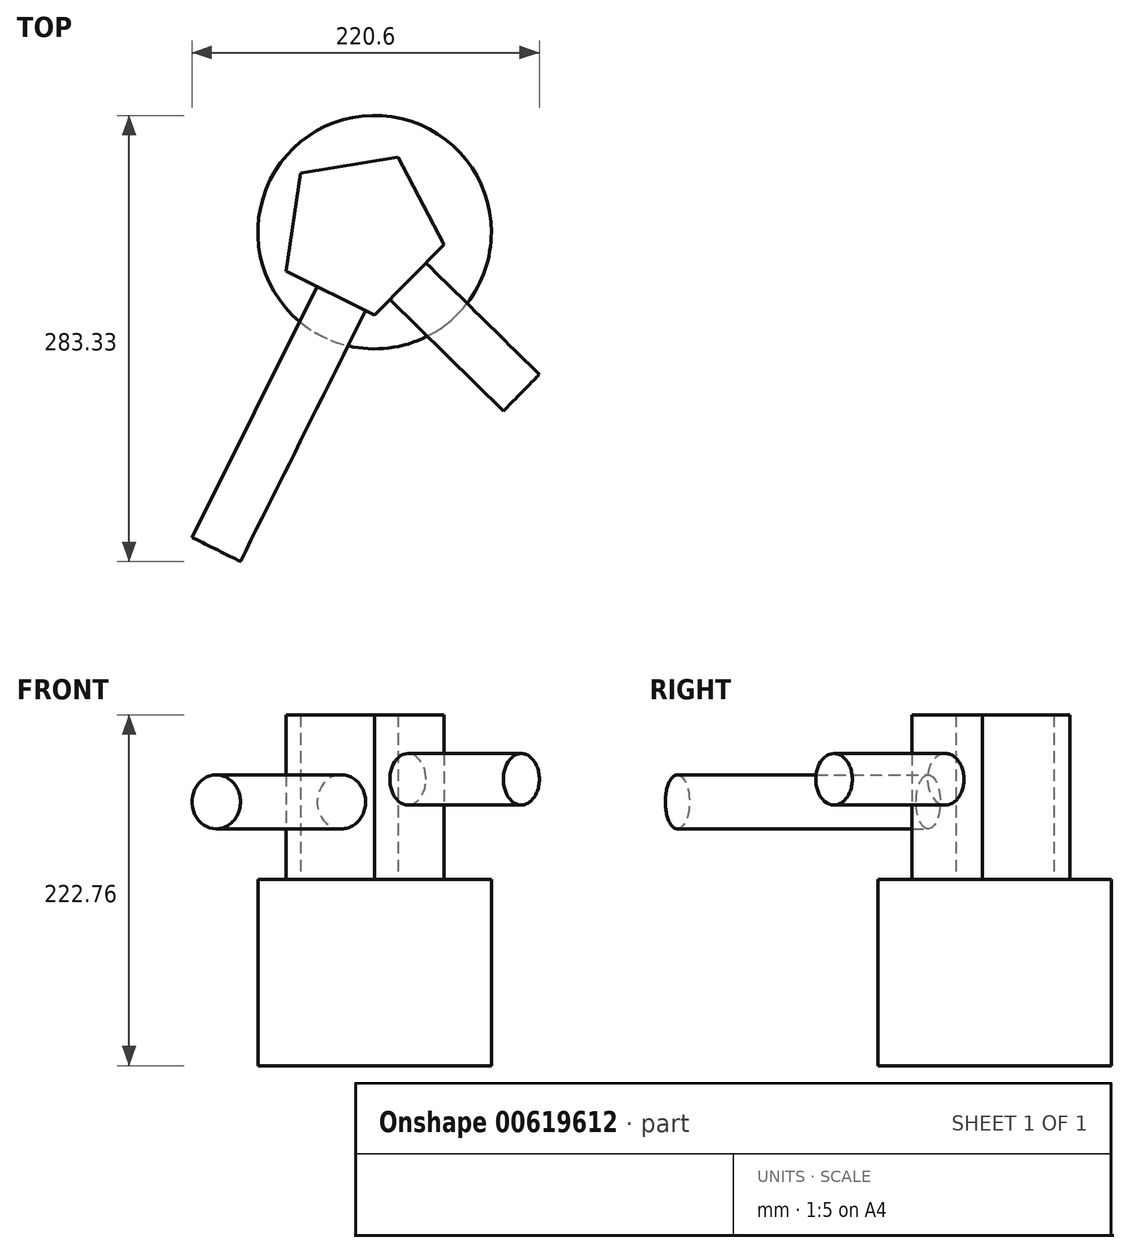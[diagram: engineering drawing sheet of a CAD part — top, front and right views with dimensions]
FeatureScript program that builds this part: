
annotation { "Feature Type Name" : "Feature", "Feature Type Description" : "" }
export const myFeature = defineFeature(function(context is Context, id is Id, definition is map)
    precondition{}
    {
        {
            var Q0;
            Q0=qCreatedBy(makeId("Top.planeOp"),FACE);
            var sketch = newSketch(context, id + "F0", { "sketchPlane" : qUnion([Q0])});
            skCircle(sketch, "E0", {"center": v(0, 0) * mm, "radius": 74.14 * mm});
            skSolve(sketch);
        }
        {
            var Q0;
            Q0=makeQuery(id+"F0.imprint","IMPRINT",FACE,{"disambiguationData":[TD([[makeQuery(id+"F0.imprint","IMPRINT",EDGE,{"derivedFrom":sQuery(id+"F0.wireOp",EDGE,"E0")}),1.0]])]});
            extrude(context, id + "F1", {"entities" : qUnion([Q0]), "depth" : 118.36 * mm, "offsetDistance" : 25.4 * mm});
        }
        {
            var Q0;
            Q0=makeQuery(id+"F1.opExtrude","CAP_FACE",FACE,{"disambiguationData":[OSD([sQuery(id+"F0.wireOp",EDGE,"E0")])],"isStart":false});
            var sketch = newSketch(context, id + "F2", { "sketchPlane" : qUnion([Q0])});
            skCircle(sketch, "E1.cCircle", {"center": v(-8.86, 0) * mm, "radius": 43.22 * mm, "construction": true});
            skLineSegment(sketch, "E1.0", {"start": v(43.98, -7.92) * mm, "end": v(-0.06, -52.7) * mm});
            skLineSegment(sketch, "E1.1", {"start": v(-0.06, -52.7) * mm, "end": v(-56.26, -24.65) * mm});
            skLineSegment(sketch, "E1.2", {"start": v(-56.26, -24.65) * mm, "end": v(-46.94, 37.47) * mm});
            skLineSegment(sketch, "E1.3", {"start": v(-46.94, 37.47) * mm, "end": v(15, 47.8) * mm});
            skLineSegment(sketch, "E1.4", {"start": v(15, 47.8) * mm, "end": v(43.98, -7.92) * mm});
            skPoint(sketch, "E1.0.midPoint", {"position": v(21.96, -30.31) * mm});
            skSolve(sketch);
        }
        {
            var Q0;
            Q0=makeQuery(id+"F2.imprint","IMPRINT",FACE,{"disambiguationData":[TD([[makeQuery(id+"F2.imprint","IMPRINT",EDGE,{"derivedFrom":sQuery(id+"F2.wireOp",EDGE,"E1.0")}),-1.0]])]});
            extrude(context, id + "F3", {"entities" : qUnion([Q0]), "operationType" : NewBodyOperationType.ADD, "depth" : 104.4 * mm, "offsetDistance" : 25.4 * mm});
        }
        {
            var Q0;
            Q0=makeQuery(id+"F3.opExtrude","SWEPT_FACE",FACE,{"disambiguationData":[OSD([sQuery(id+"F2.wireOp",EDGE,"E1.0")])]});
            var sketch = newSketch(context, id + "F4", { "sketchPlane" : qUnion([Q0])});
            skCircle(sketch, "E2", {"center": v(-7.4, 181.92) * mm, "radius": 16.32 * mm});
            skSolve(sketch);
        }
        {
            var Q0;
            Q0 = qSketchRegion(id + "F4", true);
            extrude(context, id + "F5", {"entities" : qUnion([Q0]), "operationType" : NewBodyOperationType.ADD, "depth" : 101.1 * mm, "offsetDistance" : 25.4 * mm});
        }
        {
            var Q0;
            Q0=makeQuery(id+"F3.opExtrude","SWEPT_FACE",FACE,{"disambiguationData":[OSD([sQuery(id+"F2.wireOp",EDGE,"E1.1")])]});
            var sketch = newSketch(context, id + "F6", { "sketchPlane" : qUnion([Q0])});
            skCircle(sketch, "E3", {"center": v(0, 167.6) * mm, "radius": 17.17 * mm});
            skSolve(sketch);
        }
        {
            var Q0;
            Q0 = qSketchRegion(id + "F6", true);
            extrude(context, id + "F7", {"entities" : qUnion([Q0]), "operationType" : NewBodyOperationType.ADD, "depth" : 178.05 * mm, "offsetDistance" : 25.4 * mm});
        }
    });
